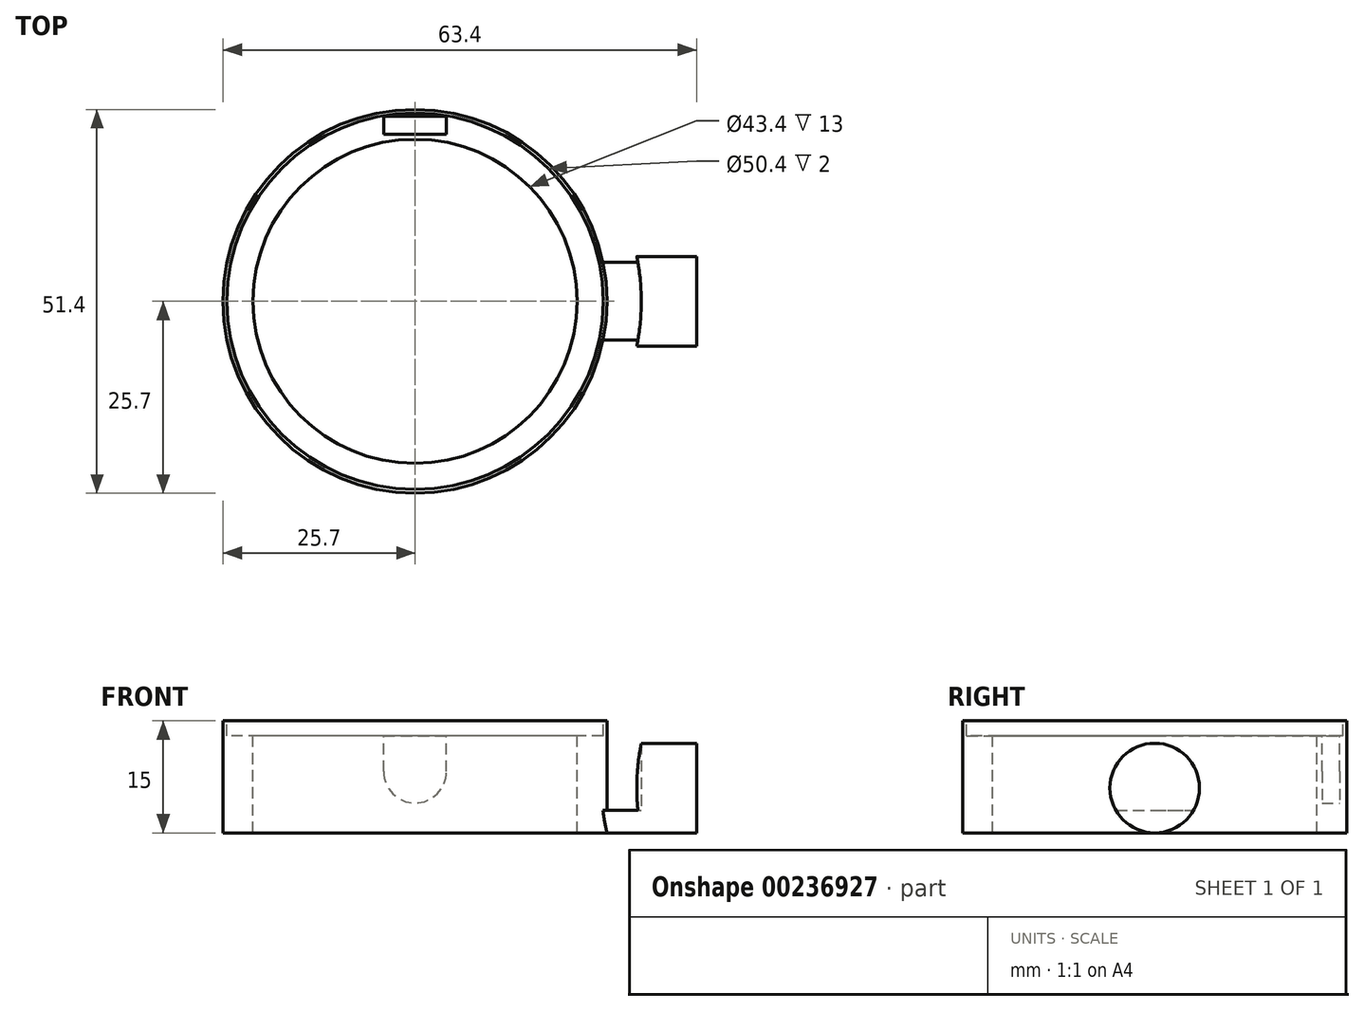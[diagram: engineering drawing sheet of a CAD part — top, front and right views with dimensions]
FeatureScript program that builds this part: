
annotation { "Feature Type Name" : "Feature", "Feature Type Description" : "" }
export const myFeature = defineFeature(function(context is Context, id is Id, definition is map)
    precondition{}
    {
        {
            var Q0;
            Q0=qCreatedBy(makeId("Top.planeOp"),FACE);
            var sketch = newSketch(context, id + "F0", { "sketchPlane" : qUnion([Q0])});
            skCircle(sketch, "E0", {"center": v(0, 0) * mm, "radius": 25.7 * mm});
            skSolve(sketch);
        }
        {
            var Q0;
            Q0 = qSketchRegion(id + "F0", true);
            extrude(context, id + "F1", {"entities" : qUnion([Q0]), "depth" : 12 * mm});
        }
        {
            var Q0;
            Q0=makeQuery(id+"F1.opExtrude","CAP_FACE",FACE,{"disambiguationData":[OSD([sQuery(id+"F0.wireOp",EDGE,"E0")])],"isStart":false});
            var sketch = newSketch(context, id + "F2", { "sketchPlane" : qUnion([Q0])});
            skCircle(sketch, "E1", {"center": v(0, 0) * mm, "radius": 21.7 * mm});
            skSolve(sketch);
        }
        {
            var Q0;
            Q0 = qSketchRegion(id + "F2", true);
            extrude(context, id + "F3", {"entities" : qUnion([Q0]), "operationType" : NewBodyOperationType.REMOVE, "oppositeDirection" : true, "depth" : 25 * mm});
        }
        {
            var Q0;
            Q0=makeQuery(id+"F1.opExtrude","CAP_FACE",FACE,{"disambiguationData":[OSD([sQuery(id+"F0.wireOp",EDGE,"E0")])],"isStart":false});
            var sketch = newSketch(context, id + "F4", { "sketchPlane" : qUnion([Q0])});
            skLineSegment(sketch, "E2.bottom", {"start": v(4.2, 22.4) * mm, "end": v(-4.2, 22.4) * mm});
            skLineSegment(sketch, "E2.top", {"start": v(4.2, 24.8) * mm, "end": v(-4.2, 24.8) * mm});
            skLineSegment(sketch, "E2.left", {"start": v(4.2, 22.4) * mm, "end": v(4.2, 24.8) * mm});
            skLineSegment(sketch, "E2.right", {"start": v(-4.2, 22.4) * mm, "end": v(-4.2, 24.8) * mm});
            skPoint(sketch, "E2.middle", {"position": v(0, 23.6) * mm});
            skSolve(sketch);
        }
        {
            var Q0;
            Q0 = qSketchRegion(id + "F4", true);
            extrude(context, id + "F5", {"entities" : qUnion([Q0]), "operationType" : NewBodyOperationType.REMOVE, "oppositeDirection" : true, "depth" : 11 * mm});
        }
        {
            var Q0;
            Q0=makeQuery(id+"F5.boolean.opBoolean","COPY",EDGE,{"derivedFrom":makeQuery(id+"F5.opExtrude","CAP_EDGE",EDGE,{"disambiguationData":[OSD([sQuery(id+"F4.wireOp",EDGE,"E2.left")])],"isStart":false})});
            var Q1;
            Q1=makeQuery(id+"F5.boolean.opBoolean","COPY",EDGE,{"derivedFrom":makeQuery(id+"F5.opExtrude","CAP_EDGE",EDGE,{"disambiguationData":[OSD([sQuery(id+"F4.wireOp",EDGE,"E2.right")])],"isStart":false})});
            fillet(context, id + "F6", {"entities" : qUnion([Q0, Q1]), "radius" : 4.2 * mm, "tangentPropagation" : true, "allowEdgeOverflow" : false});
        }
        {
            var Q0;
            Q0=makeQuery(id+"F1.opExtrude","CAP_FACE",FACE,{"disambiguationData":[OSD([sQuery(id+"F0.wireOp",EDGE,"E0")])],"isStart":true});
            var sketch = newSketch(context, id + "F7", { "sketchPlane" : qUnion([Q0])});
            skCircle(sketch, "E3.0", {"center": v(0, 0) * mm, "radius": 25.7 * mm});
            skCircle(sketch, "E4.0", {"center": v(0, 0) * mm, "radius": 21.7 * mm});
            skLineSegment(sketch, "E5.bottom", {"start": v(13.7, 6) * mm, "end": v(37.7, 6) * mm});
            skLineSegment(sketch, "E5.top", {"start": v(13.7, -6) * mm, "end": v(37.7, -6) * mm});
            skLineSegment(sketch, "E5.left", {"start": v(13.7, 6) * mm, "end": v(13.7, -6) * mm});
            skLineSegment(sketch, "E5.right", {"start": v(37.7, 6) * mm, "end": v(37.7, -6) * mm});
            skPoint(sketch, "E5.middle", {"position": v(25.7, 0) * mm});
            skSolve(sketch);
        }
        {
            var Q0;
            {var subQ0=sQuery(id+"F7.wireOp",EDGE,"E5.bottom");var subQ1=sQuery(id+"F7.wireOp",EDGE,"E3.0");var subQ2=makeQuery(id+"F7.imprint","INTERSECT",VERTEX,{"derivedFrom":[subQ1,subQ0]});Q0=makeQuery(id+"F7.imprint","IMPRINT",FACE,{"disambiguationData":[TD([[makeQuery(id+"F7.imprint","IMPRINT",EDGE,{"disambiguationData":[TD([[subQ2,1.0]])],"derivedFrom":subQ1}),-1.0]])]});}
            var Q1;
            {var subQ0=sQuery(id+"F7.wireOp",EDGE,"E5.bottom");var subQ1=sQuery(id+"F7.wireOp",EDGE,"E3.0");var subQ2=makeQuery(id+"F7.imprint","INTERSECT",VERTEX,{"derivedFrom":[subQ1,subQ0]});Q1=makeQuery(id+"F7.imprint","IMPRINT",FACE,{"disambiguationData":[TD([[makeQuery(id+"F7.imprint","IMPRINT",EDGE,{"disambiguationData":[TD([[subQ2,-1.0]])],"derivedFrom":subQ1}),-1.0]])]});}
            var Q2;
            {var subQ5=sQuery(id+"F7.wireOp",EDGE,"E5.right");Q2=makeQuery(id+"F7.imprint","IMPRINT",FACE,{"disambiguationData":[TD([[makeQuery(id+"F7.imprint","IMPRINT",EDGE,{"derivedFrom":subQ5}),-1.0]])]});}
            extrude(context, id + "F8", {"entities" : qUnion([Q0, Q1, Q2]), "operationType" : NewBodyOperationType.ADD, "depth" : 3 * mm});
        }
        {
            var Q0;
            Q0=makeQuery(id+"F8.opExtrude","CAP_FACE",FACE,{"disambiguationData":[OSD([sQuery(id+"F7.wireOp",EDGE,"E3.0"),sQuery(id+"F7.wireOp",EDGE,"E4.0"),sQuery(id+"F7.wireOp",EDGE,"E5.bottom"),sQuery(id+"F7.wireOp",EDGE,"E5.top"),sQuery(id+"F7.wireOp",EDGE,"E5.right")])],"isStart":true});
            var sketch = newSketch(context, id + "F9", { "sketchPlane" : qUnion([Q0])});
            skArc(sketch, "E6.0.0", {"start": v(24.99, 6) * mm, "mid": v(25.7, 0) * mm, "end": v(24.99, -6) * mm});
            skLineSegment(sketch, "E6.0.1", {"start": v(24.99, -6) * mm, "end": v(37.7, -6) * mm});
            skLineSegment(sketch, "E6.0.2", {"start": v(37.7, -6) * mm, "end": v(37.7, 6) * mm});
            skLineSegment(sketch, "E6.0.3", {"start": v(37.7, 6) * mm, "end": v(24.99, 6) * mm});
            skCircle(sketch, "E7", {"center": v(0, 0) * mm, "radius": 30.3 * mm});
            skSolve(sketch);
        }
        {
            var Q0;
            {var subQ0=sQuery(id+"F9.wireOp",EDGE,"E6.0.2");Q0=makeQuery(id+"F9.imprint","IMPRINT",FACE,{"disambiguationData":[TD([[makeQuery(id+"F9.imprint","IMPRINT",EDGE,{"derivedFrom":subQ0}),1.0]])]});}
            extrude(context, id + "F10", {"entities" : qUnion([Q0]), "operationType" : NewBodyOperationType.ADD, "depth" : 9 * mm});
        }
        {
            var Q0;
            Q0=makeQuery(id+"F1.opExtrude","CAP_FACE",FACE,{"disambiguationData":[OSD([sQuery(id+"F0.wireOp",EDGE,"E0")])],"isStart":false});
            var sketch = newSketch(context, id + "F11", { "sketchPlane" : qUnion([Q0])});
            skCircle(sketch, "E8", {"center": v(0, 0) * mm, "radius": 25.2 * mm});
            skSolve(sketch);
        }
        {
            var Q0;
            Q0 = qSketchRegion(id + "F11", true);
            extrude(context, id + "F12", {"entities" : qUnion([Q0]), "operationType" : NewBodyOperationType.REMOVE, "oppositeDirection" : true, "depth" : 2 * mm});
        }
        {
            var Q0;
            Q0=makeQuery(id+"F8.opExtrude","CAP_EDGE",EDGE,{"disambiguationData":[OSD([sQuery(id+"F7.wireOp",EDGE,"E5.bottom")])],"isStart":false});
            var Q1;
            Q1=makeQuery(id+"F8.opExtrude","CAP_EDGE",EDGE,{"disambiguationData":[OSD([sQuery(id+"F7.wireOp",EDGE,"E5.top")])],"isStart":false});
            var Q2;
            Q2=makeQuery(id+"F10.opExtrude","CAP_EDGE",EDGE,{"disambiguationData":[OSD([sQuery(id+"F9.wireOp",EDGE,"E6.0.1")])],"isStart":false});
            var Q3;
            Q3=makeQuery(id+"F10.opExtrude","CAP_EDGE",EDGE,{"disambiguationData":[OSD([sQuery(id+"F9.wireOp",EDGE,"E6.0.3")])],"isStart":false});
            fillet(context, id + "F13", {"entities" : qUnion([Q0, Q1, Q2, Q3]), "radius" : 6 * mm, "tangentPropagation" : true, "allowEdgeOverflow" : false});
        }
    });
